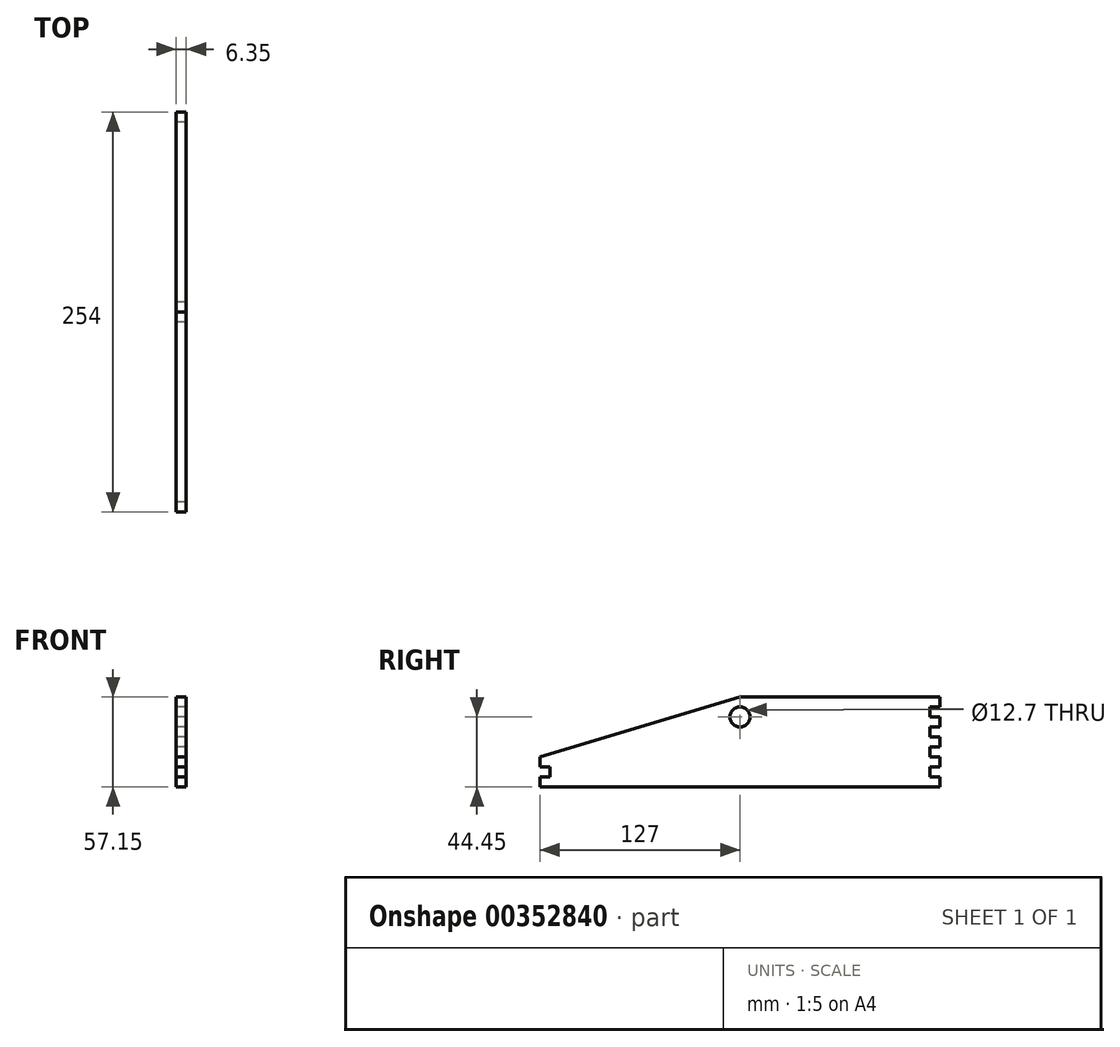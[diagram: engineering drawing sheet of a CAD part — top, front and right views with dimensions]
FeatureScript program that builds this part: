
annotation { "Feature Type Name" : "Feature", "Feature Type Description" : "" }
export const myFeature = defineFeature(function(context is Context, id is Id, definition is map)
    precondition{}
    {
        {
            var Q0;
            Q0=qCreatedBy(makeId("Right.planeOp"),FACE);
            var sketch = newSketch(context, id + "F0", { "sketchPlane" : qUnion([Q0])});
            skLineSegment(sketch, "E0.bottom", {"start": v(0, 0) * mm, "end": v(254, 0) * mm});
            skLineSegment(sketch, "E0.top", {"start": v(127, 57.15) * mm, "end": v(254, 57.15) * mm});
            skLineSegment(sketch, "E0.left", {"start": v(0, 0) * mm, "end": v(0, 6.35) * mm});
            skLineSegment(sketch, "E0.right", {"start": v(254, 0) * mm, "end": v(254, 6.35) * mm});
            skLineSegment(sketch, "E1", {"start": v(127, 57.15) * mm, "end": v(127, 0) * mm, "construction": true});
            skCircle(sketch, "E2", {"center": v(127, 44.45) * mm, "radius": 6.35 * mm});
            skLineSegment(sketch, "E3", {"start": v(127, 57.15) * mm, "end": v(0, 19.05) * mm});
            skPoint(sketch, "E4.orphan", {"position": v(0, 57.15) * mm});
            skLineSegment(sketch, "E5.bottom", {"start": v(254, 6.35) * mm, "end": v(247.65, 6.35) * mm});
            skLineSegment(sketch, "E5.top", {"start": v(254, 12.7) * mm, "end": v(247.65, 12.7) * mm});
            skLineSegment(sketch, "E5.right", {"start": v(247.65, 6.35) * mm, "end": v(247.65, 12.7) * mm});
            skLineSegment(sketch, "E6.0.1.0", {"start": v(254, 25.4) * mm, "end": v(247.65, 25.4) * mm});
            skLineSegment(sketch, "E6.0.1.1", {"start": v(254, 19.05) * mm, "end": v(247.65, 19.05) * mm});
            skLineSegment(sketch, "E6.0.1.2", {"start": v(247.65, 19.05) * mm, "end": v(247.65, 25.4) * mm});
            skLineSegment(sketch, "E6.direction1", {"start": v(247.65, 12.7) * mm, "end": v(273.05, 12.7) * mm, "construction": true});
            skLineSegment(sketch, "E6.direction2", {"start": v(247.65, 12.7) * mm, "end": v(247.65, 25.4) * mm, "construction": true});
            skLineSegment(sketch, "E7.bottom", {"start": v(0, 6.35) * mm, "end": v(6.35, 6.35) * mm});
            skLineSegment(sketch, "E7.top", {"start": v(0, 12.7) * mm, "end": v(6.35, 12.7) * mm});
            skLineSegment(sketch, "E7.right", {"start": v(6.35, 6.35) * mm, "end": v(6.35, 12.7) * mm});
            skLineSegment(sketch, "E8.0.0.2", {"start": v(254, 38.1) * mm, "end": v(247.65, 38.1) * mm});
            skLineSegment(sketch, "E8.3.0.2", {"start": v(254, 31.75) * mm, "end": v(247.65, 31.75) * mm});
            skLineSegment(sketch, "E8.6.0.2", {"start": v(247.65, 31.75) * mm, "end": v(247.65, 38.1) * mm});
            skLineSegment(sketch, "E8.0.0.3", {"start": v(254, 50.8) * mm, "end": v(247.65, 50.8) * mm});
            skLineSegment(sketch, "E8.3.0.3", {"start": v(254, 44.45) * mm, "end": v(247.65, 44.45) * mm});
            skLineSegment(sketch, "E8.6.0.3", {"start": v(247.65, 44.45) * mm, "end": v(247.65, 50.8) * mm});
            skLineSegment(sketch, "E9.trimOffspring", {"start": v(0, 12.7) * mm, "end": v(0, 19.05) * mm});
            skLineSegment(sketch, "E10.trimOffspring", {"start": v(254, 12.7) * mm, "end": v(254, 19.05) * mm});
            skLineSegment(sketch, "E11.trimOffspring", {"start": v(254, 25.4) * mm, "end": v(254, 31.75) * mm});
            skLineSegment(sketch, "E12.trimOffspring", {"start": v(254, 38.1) * mm, "end": v(254, 44.45) * mm});
            skLineSegment(sketch, "E13.trimOffspring", {"start": v(254, 50.8) * mm, "end": v(254, 57.15) * mm});
            skSolve(sketch);
        }
        {
            var Q0;
            Q0 = qSketchRegion(id + "F0", true);
            extrude(context, id + "F1", {"entities" : qUnion([Q0]), "depth" : 6.35 * mm});
        }
    });
